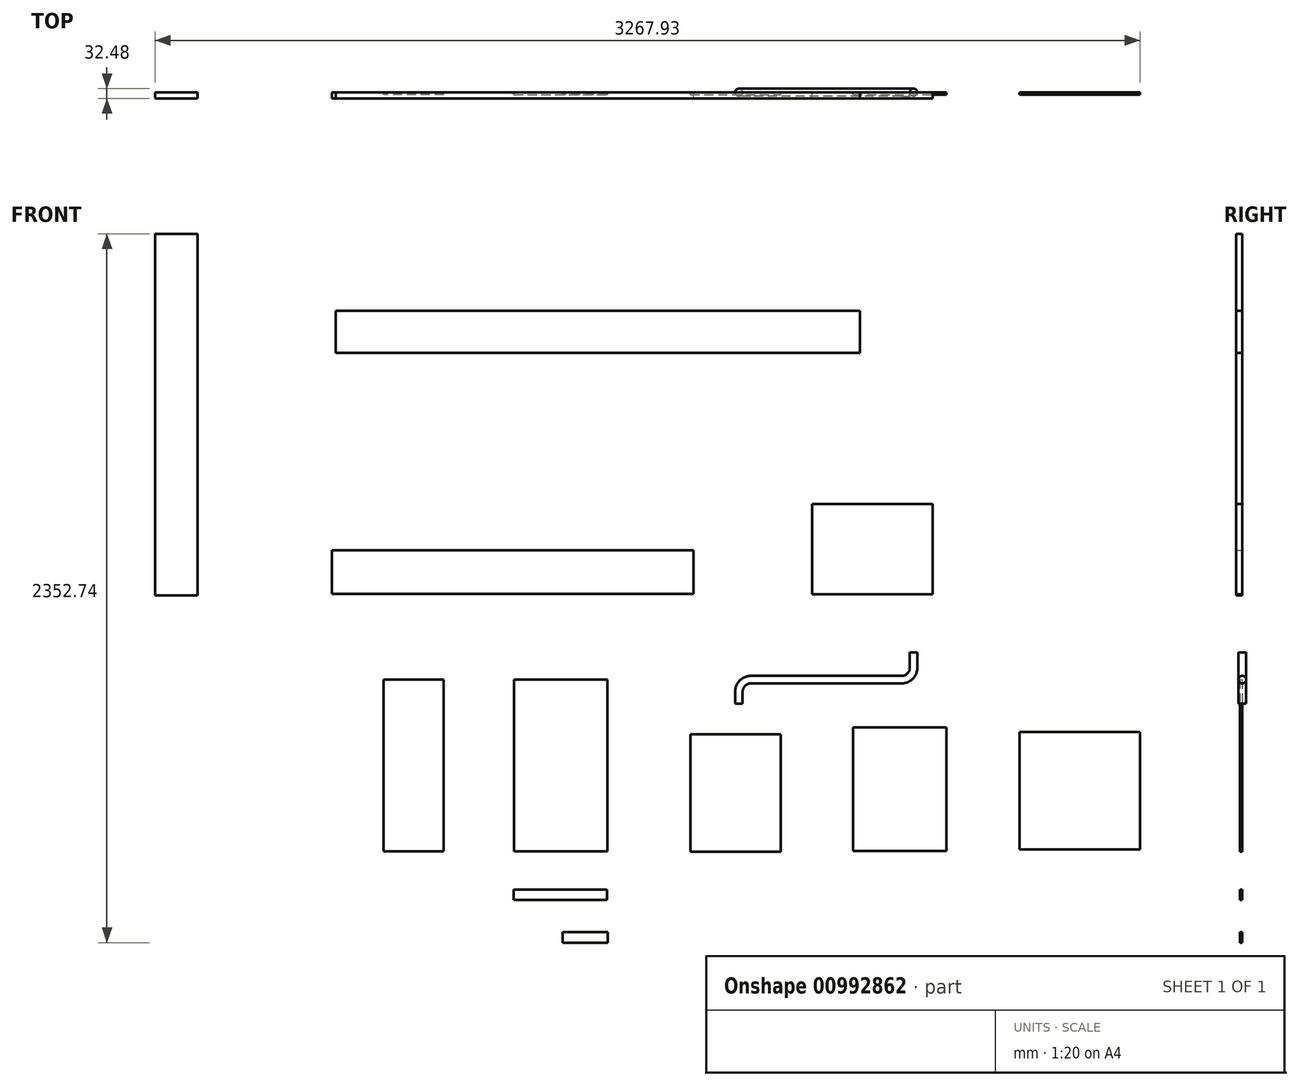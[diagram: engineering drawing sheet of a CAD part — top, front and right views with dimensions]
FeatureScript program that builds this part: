
annotation { "Feature Type Name" : "Feature", "Feature Type Description" : "" }
export const myFeature = defineFeature(function(context is Context, id is Id, definition is map)
    precondition{}
    {
        {
            var Q0;
            Q0=qCreatedBy(makeId("Right.planeOp"),FACE);
            var sketch = newSketch(context, id + "F0", { "sketchPlane" : qUnion([Q0])});
            skCircle(sketch, "E0", {"center": v(0, 0) * mm, "radius": 12.48 * mm});
            skSolve(sketch);
        }
        {
            var Q0;
            Q0 = qSketchRegion(id + "F0", true);
            extrude(context, id + "F1", {"entities" : qUnion([Q0]), "depth" : 500 * mm, "offsetDistance" : 25 * mm});
        }
        {
            var Q0;
            Q0=qCreatedBy(makeId("Front.planeOp"),FACE);
            var sketch = newSketch(context, id + "F2", { "sketchPlane" : qUnion([Q0])});
            skLineSegment(sketch, "E1.bottom", {"start": v(203.77, 583.24) * mm, "end": v(603.77, 583.24) * mm});
            skLineSegment(sketch, "E1.top", {"start": v(203.77, 283.24) * mm, "end": v(603.77, 283.24) * mm});
            skLineSegment(sketch, "E1.left", {"start": v(203.77, 583.24) * mm, "end": v(203.77, 283.24) * mm});
            skLineSegment(sketch, "E1.right", {"start": v(603.77, 583.24) * mm, "end": v(603.77, 283.24) * mm});
            skSolve(sketch);
        }
        {
            var Q0;
            Q0 = qSketchRegion(id + "F2", true);
            extrude(context, id + "F3", {"entities" : qUnion([Q0]), "depth" : 20 * mm, "offsetDistance" : 25 * mm});
        }
        {
            var Q0;
            Q0=qCreatedBy(makeId("Front.planeOp"),FACE);
            var sketch = newSketch(context, id + "F4", { "sketchPlane" : qUnion([Q0])});
            skLineSegment(sketch, "E2.bottom", {"start": v(-1390.36, 429.3) * mm, "end": v(-190.36, 429.3) * mm});
            skLineSegment(sketch, "E2.top", {"start": v(-1390.36, 284.3) * mm, "end": v(-190.36, 284.3) * mm});
            skLineSegment(sketch, "E2.left", {"start": v(-1390.36, 429.3) * mm, "end": v(-1390.36, 284.3) * mm});
            skLineSegment(sketch, "E2.right", {"start": v(-190.36, 429.3) * mm, "end": v(-190.36, 284.3) * mm});
            skSolve(sketch);
        }
        {
            var Q0;
            Q0 = qSketchRegion(id + "F4", true);
            extrude(context, id + "F5", {"entities" : qUnion([Q0]), "depth" : 20 * mm, "offsetDistance" : 25 * mm});
        }
        {
            var Q0;
            Q0=qCreatedBy(makeId("Front.planeOp"),FACE);
            var sketch = newSketch(context, id + "F6", { "sketchPlane" : qUnion([Q0])});
            skLineSegment(sketch, "E3.bottom", {"start": v(-1378.01, 1224.67) * mm, "end": v(361.99, 1224.67) * mm});
            skLineSegment(sketch, "E3.top", {"start": v(-1378.01, 1084.67) * mm, "end": v(361.99, 1084.67) * mm});
            skLineSegment(sketch, "E3.left", {"start": v(-1378.01, 1224.67) * mm, "end": v(-1378.01, 1084.67) * mm});
            skLineSegment(sketch, "E3.right", {"start": v(361.99, 1224.67) * mm, "end": v(361.99, 1084.67) * mm});
            skLineSegment(sketch, "E4.bottom", {"start": v(-1977.01, 1479.67) * mm, "end": v(-1837.01, 1479.67) * mm});
            skLineSegment(sketch, "E4.top", {"start": v(-1977.01, 279.67) * mm, "end": v(-1837.01, 279.67) * mm});
            skLineSegment(sketch, "E4.left", {"start": v(-1977.01, 1479.67) * mm, "end": v(-1977.01, 279.67) * mm});
            skLineSegment(sketch, "E4.right", {"start": v(-1837.01, 1479.67) * mm, "end": v(-1837.01, 279.67) * mm});
            skSolve(sketch);
        }
        {
            var Q0;
            Q0=makeQuery(id+"F6.imprint","IMPRINT",FACE,{"disambiguationData":[TD([[makeQuery(id+"F6.imprint","IMPRINT",EDGE,{"derivedFrom":sQuery(id+"F6.wireOp",EDGE,"E3.bottom")}),-1.0]])]});
            extrude(context, id + "F7", {"entities" : qUnion([Q0]), "depth" : 20 * mm, "offsetDistance" : 25 * mm});
        }
        {
            var Q0;
            Q0=makeQuery(id+"F6.imprint","IMPRINT",FACE,{"disambiguationData":[TD([[makeQuery(id+"F6.imprint","IMPRINT",EDGE,{"derivedFrom":sQuery(id+"F6.wireOp",EDGE,"E4.top")}),1.0]])]});
            extrude(context, id + "F8", {"entities" : qUnion([Q0]), "depth" : 20 * mm, "offsetDistance" : 25 * mm});
        }
        {
            var Q0;
            Q0=qCreatedBy(makeId("Front.planeOp"),FACE);
            var sketch = newSketch(context, id + "F9", { "sketchPlane" : qUnion([Q0])});
            skLineSegment(sketch, "E5.bottom", {"start": v(-786.13, 0) * mm, "end": v(-476.13, 0) * mm});
            skLineSegment(sketch, "E5.top", {"start": v(-786.13, -570) * mm, "end": v(-476.13, -570) * mm});
            skLineSegment(sketch, "E5.left", {"start": v(-786.13, 0) * mm, "end": v(-786.13, -570) * mm});
            skLineSegment(sketch, "E5.right", {"start": v(-476.13, 0) * mm, "end": v(-476.13, -570) * mm});
            skSolve(sketch);
        }
        {
            var Q0;
            Q0=makeQuery(id+"F9.imprint","IMPRINT",FACE,{"disambiguationData":[TD([[makeQuery(id+"F9.imprint","IMPRINT",EDGE,{"derivedFrom":sQuery(id+"F9.wireOp",EDGE,"E5.bottom")}),-1.0]])]});
            extrude(context, id + "F10", {"entities" : qUnion([Q0]), "depth" : 7.5 * mm, "offsetDistance" : 25 * mm});
        }
        {
            var Q0;
            Q0=qCreatedBy(makeId("Front.planeOp"),FACE);
            var sketch = newSketch(context, id + "F11", { "sketchPlane" : qUnion([Q0])});
            skLineSegment(sketch, "E6.bottom", {"start": v(-1019.6, 0) * mm, "end": v(-1219.6, 0) * mm});
            skLineSegment(sketch, "E6.top", {"start": v(-1019.6, -570) * mm, "end": v(-1219.6, -570) * mm});
            skLineSegment(sketch, "E6.left", {"start": v(-1019.6, 0) * mm, "end": v(-1019.6, -570) * mm});
            skLineSegment(sketch, "E6.right", {"start": v(-1219.6, 0) * mm, "end": v(-1219.6, -570) * mm});
            skSolve(sketch);
        }
        {
            var Q0;
            Q0=makeQuery(id+"F11.imprint","IMPRINT",FACE,{"disambiguationData":[TD([[makeQuery(id+"F11.imprint","IMPRINT",EDGE,{"derivedFrom":sQuery(id+"F11.wireOp",EDGE,"E6.bottom")}),1.0]])]});
            extrude(context, id + "F12", {"entities" : qUnion([Q0]), "depth" : 7.5 * mm, "offsetDistance" : 25 * mm});
        }
        {
            var Q0;
            Q0=qCreatedBy(makeId("Front.planeOp"),FACE);
            var sketch = newSketch(context, id + "F13", { "sketchPlane" : qUnion([Q0])});
            skLineSegment(sketch, "E7.bottom", {"start": v(-788, -696.79) * mm, "end": v(-478, -696.79) * mm});
            skLineSegment(sketch, "E7.top", {"start": v(-788, -731.79) * mm, "end": v(-478, -731.79) * mm});
            skLineSegment(sketch, "E7.left", {"start": v(-788, -696.79) * mm, "end": v(-788, -731.79) * mm});
            skLineSegment(sketch, "E7.right", {"start": v(-478, -696.79) * mm, "end": v(-478, -731.79) * mm});
            skSolve(sketch);
        }
        {
            var Q0;
            Q0=makeQuery(id+"F13.imprint","IMPRINT",FACE,{"disambiguationData":[TD([[makeQuery(id+"F13.imprint","IMPRINT",EDGE,{"derivedFrom":sQuery(id+"F13.wireOp",EDGE,"E7.bottom")}),-1.0]])]});
            extrude(context, id + "F14", {"entities" : qUnion([Q0]), "depth" : 7.5 * mm, "offsetDistance" : 25 * mm});
        }
        {
            var Q0;
            Q0=qCreatedBy(makeId("Front.planeOp"),FACE);
            var sketch = newSketch(context, id + "F15", { "sketchPlane" : qUnion([Q0])});
            skLineSegment(sketch, "E8.bottom", {"start": v(-200.6, -181.1) * mm, "end": v(99.4, -181.1) * mm});
            skLineSegment(sketch, "E8.top", {"start": v(-200.6, -571.1) * mm, "end": v(99.4, -571.1) * mm});
            skLineSegment(sketch, "E8.left", {"start": v(-200.6, -181.1) * mm, "end": v(-200.6, -571.1) * mm});
            skLineSegment(sketch, "E8.right", {"start": v(99.4, -181.1) * mm, "end": v(99.4, -571.1) * mm});
            skSolve(sketch);
        }
        {
            var Q0;
            Q0=makeQuery(id+"F15.imprint","IMPRINT",FACE,{"disambiguationData":[TD([[makeQuery(id+"F15.imprint","IMPRINT",EDGE,{"derivedFrom":sQuery(id+"F15.wireOp",EDGE,"E8.bottom")}),-1.0]])]});
            extrude(context, id + "F16", {"entities" : qUnion([Q0]), "depth" : 7.5 * mm, "offsetDistance" : 25 * mm});
        }
        {
            var Q0;
            Q0=qCreatedBy(makeId("Front.planeOp"),FACE);
            var sketch = newSketch(context, id + "F17", { "sketchPlane" : qUnion([Q0])});
            skLineSegment(sketch, "E9.bottom", {"start": v(339.03, -158.9) * mm, "end": v(649.03, -158.9) * mm});
            skLineSegment(sketch, "E9.top", {"start": v(339.03, -568.9) * mm, "end": v(649.03, -568.9) * mm});
            skLineSegment(sketch, "E9.left", {"start": v(339.03, -158.9) * mm, "end": v(339.03, -568.9) * mm});
            skLineSegment(sketch, "E9.right", {"start": v(649.03, -158.9) * mm, "end": v(649.03, -568.9) * mm});
            skSolve(sketch);
        }
        {
            var Q0;
            Q0 = qSketchRegion(id + "F17", true);
            extrude(context, id + "F18", {"entities" : qUnion([Q0]), "depth" : 7.5 * mm, "offsetDistance" : 25 * mm});
        }
        {
            var Q0;
            Q0=qCreatedBy(makeId("Front.planeOp"),FACE);
            var sketch = newSketch(context, id + "F19", { "sketchPlane" : qUnion([Q0])});
            skLineSegment(sketch, "E10.bottom", {"start": v(890.92, -563.42) * mm, "end": v(1290.92, -563.42) * mm});
            skLineSegment(sketch, "E10.top", {"start": v(890.92, -173.42) * mm, "end": v(1290.92, -173.42) * mm});
            skLineSegment(sketch, "E10.left", {"start": v(890.92, -563.42) * mm, "end": v(890.92, -173.42) * mm});
            skLineSegment(sketch, "E10.right", {"start": v(1290.92, -563.42) * mm, "end": v(1290.92, -173.42) * mm});
            skSolve(sketch);
        }
        {
            var Q0;
            Q0=makeQuery(id+"F19.imprint","IMPRINT",FACE,{"disambiguationData":[TD([[makeQuery(id+"F19.imprint","IMPRINT",EDGE,{"derivedFrom":sQuery(id+"F19.wireOp",EDGE,"E10.bottom")}),1.0]])]});
            extrude(context, id + "F20", {"entities" : qUnion([Q0]), "depth" : 7.5 * mm, "offsetDistance" : 25 * mm});
        }
        {
            var Q0;
            Q0=qCreatedBy(makeId("Front.planeOp"),FACE);
            var sketch = newSketch(context, id + "F21", { "sketchPlane" : qUnion([Q0])});
            skLineSegment(sketch, "E11.top", {"start": v(0, -40) * mm, "end": v(-40, -40) * mm});
            skLineSegment(sketch, "E11.left", {"start": v(0, 0) * mm, "end": v(0, -40) * mm});
            skArc(sketch, "E12", {"start": v(0, 0) * mm, "mid": v(-28.28, -11.72) * mm, "end": v(-40, -40) * mm});
            skLineSegment(sketch, "E13", {"start": v(-40, -40) * mm, "end": v(-40, -80) * mm});
            skLineSegment(sketch, "E14", {"start": v(0, 0) * mm, "end": v(500, 0) * mm});
            skLineSegment(sketch, "E15.top", {"start": v(500, 40) * mm, "end": v(540, 40) * mm});
            skLineSegment(sketch, "E15.left", {"start": v(500, 0) * mm, "end": v(500, 40) * mm});
            skArc(sketch, "E16", {"start": v(500, 0) * mm, "mid": v(528.28, 11.72) * mm, "end": v(540, 40) * mm});
            skLineSegment(sketch, "E17", {"start": v(540, 40) * mm, "end": v(540, 90) * mm});
            skSolve(sketch);
        }
        {
            var Q0;
            Q0=makeQuery(id+"F1.opExtrude","CAP_FACE",FACE,{"disambiguationData":[OSD([sQuery(id+"F0.wireOp",EDGE,"E0")])],"isStart":true});
            var Q1;
            Q1=sQuery(id+"F21.wireOp",EDGE,"E12");
            var Q2;
            Q2=sQuery(id+"F21.wireOp",EDGE,"E13");
            sweep(context, id + "F22", {"operationType" : NewBodyOperationType.ADD, "profiles" : qUnion([Q0]), "path" : qUnion([Q1, Q2])});
        }
        {
            var Q0;
            Q0=makeQuery(id+"F1.opExtrude","CAP_FACE",FACE,{"disambiguationData":[OSD([sQuery(id+"F0.wireOp",EDGE,"E0")])],"isStart":false});
            var Q1;
            Q1=sQuery(id+"F21.wireOp",EDGE,"E16");
            var Q2;
            Q2=sQuery(id+"F21.wireOp",EDGE,"E17");
            sweep(context, id + "F23", {"operationType" : NewBodyOperationType.ADD, "profiles" : qUnion([Q0]), "path" : qUnion([Q1, Q2])});
        }
        {
            var Q0;
            Q0=qCreatedBy(makeId("Front.planeOp"),FACE);
            var sketch = newSketch(context, id + "F24", { "sketchPlane" : qUnion([Q0])});
            skLineSegment(sketch, "E18.bottom", {"start": v(-475.1, -873.07) * mm, "end": v(-625.1, -873.07) * mm});
            skLineSegment(sketch, "E18.top", {"start": v(-475.1, -838.07) * mm, "end": v(-625.1, -838.07) * mm});
            skLineSegment(sketch, "E18.left", {"start": v(-475.1, -873.07) * mm, "end": v(-475.1, -838.07) * mm});
            skLineSegment(sketch, "E18.right", {"start": v(-625.1, -873.07) * mm, "end": v(-625.1, -838.07) * mm});
            skSolve(sketch);
        }
        {
            var Q0;
            Q0=makeQuery(id+"F24.imprint","IMPRINT",FACE,{"disambiguationData":[TD([[makeQuery(id+"F24.imprint","IMPRINT",EDGE,{"derivedFrom":sQuery(id+"F24.wireOp",EDGE,"E18.bottom")}),-1.0]])]});
            extrude(context, id + "F25", {"entities" : qUnion([Q0]), "depth" : 7.5 * mm, "offsetDistance" : 25 * mm});
        }
    });
